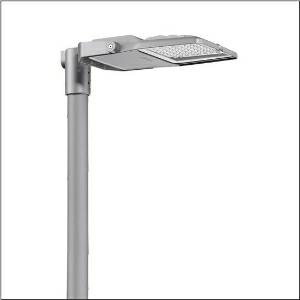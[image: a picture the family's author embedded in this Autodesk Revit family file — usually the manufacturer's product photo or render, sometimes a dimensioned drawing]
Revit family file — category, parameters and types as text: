
# Revit family: floodlight_fl_21_mini___pl33t_5xa7775c2f3a_8bfe
name_source: partatom
category: Lighting Fixtures
units: mm (PartAtom-declared; Revit-internal decimal feet)

## family parameters
Cut with Voids When Loaded = No
Host = Face
Light Source = No
Part Type = Normal
Room Calculation Point = No
Round Connector Dimension = Use Diameter
Shared = No

## types (1)
- --- (1 x LED, 12050 lm, 89 W, 3000K)
    Apparent Load = 89 VA
    CIE Flux Codes = 26 75 99 100 100
    Color Rendering = 70
    Color Temperature = 3000K
    Default Elevation = 1800 mm
    Description = Floodlight FL 21 mini, floodlight, primary light control with lens, of PMMA, primary optical cover: protective disc, of toughened safety glass, transparent, light distribution: PL33T, light emission: direct distribution, installation type: surface-mounted, LED, High Power LED, rated luminous flux: 12.050lm, luminous efficacy: 135lm/W, light colour: 730, colour temperature: 3000K, control gear: Smart Interface (Zhaga), control: flexible luminous flux parameterisation, time-dependent luminous flux control, constant luminous flux control, overheat protection, pre-setting: logarithmic dimming characteristic, with terminal, 6-pole, mains connection: 220..240V, AC, 50/60Hz, start of lifetime: 89W, end of service life: 94W, reduction: 43W, luminaire housing, of diecast aluminium, powder-coated, Siteco® metallic grey (DB 702S), corrosivity category C5 mid according to DIN EN ISO 12944, suitable for swimming pools, chlorine-resistant, sealing non-destructively replaceable, please order mast flange separately, mast bracket, of steel, galvanised, powder-coated, Siteco® metallic grey (DB 702S), Smart Interface above, protection rating (complete): IP66, insulation class (complete): insulation class II (safety insulation), certification: CE, ENEC, VDE, protection symbol: D, impact resistance: IK08, permissible operating ambient temperature: -40..+40°C, permissible operating ambient temperature for outdoor applications: -40..+50°C, standard: DIN EN 12944, LABS conformity tested according to VDMA 24364:2018-05, packaging unit: 1 piece

Light Distribution: PL33T
    Height = 70 mm
    Lamp = 1 x LED
    Lamp Light Flux = 12050 lm
    Lamp Power = 89 W
    Lamp count = 1
    Length = 485 mm
    Luminous efficacy = 135 lm/W
    Manufacturer = Siteco
    ModVariant = No
    Model = 5XA7775C2F3A
    Number of Poles = 1
    OnlyDefault = Yes
    Power Factor = 1
    Product Name = Floodlight FL 21 mini | PL33T
    Product group = floodlight | pylon annexe
    ProductGroupID = 6200
    Protection Class = Protection class II
    Protection Degree = IP 66
    RLX_Detail_Level = 1
    RLX_Emergency_Light_Flux = 0 lm
    RLX_Emergency_Type = 0
    RLX_Emergency_Type_DB = No
    RlxData = <blob elided: 100797 chars, md5=e90d7c63>
    Socket = socket
    Standby Power = 0 W
    System Light Flux = 12050 lm
    System Power = 89 W
    Type Comments = factory setting: luminous flux: 100 % | dim-lin: 254 | 456 mA
    Type Image = l_1007125.jpg
    URL = http://relux.com
    VarID = @adj_148542
    Voltage = 0 V
    Weight = 0.00 kg
    Width = 337 mm

## geometry (parser evidence)
native form markers: Blend x4, Sweep x11
no freeform markers — native parametric forms only
